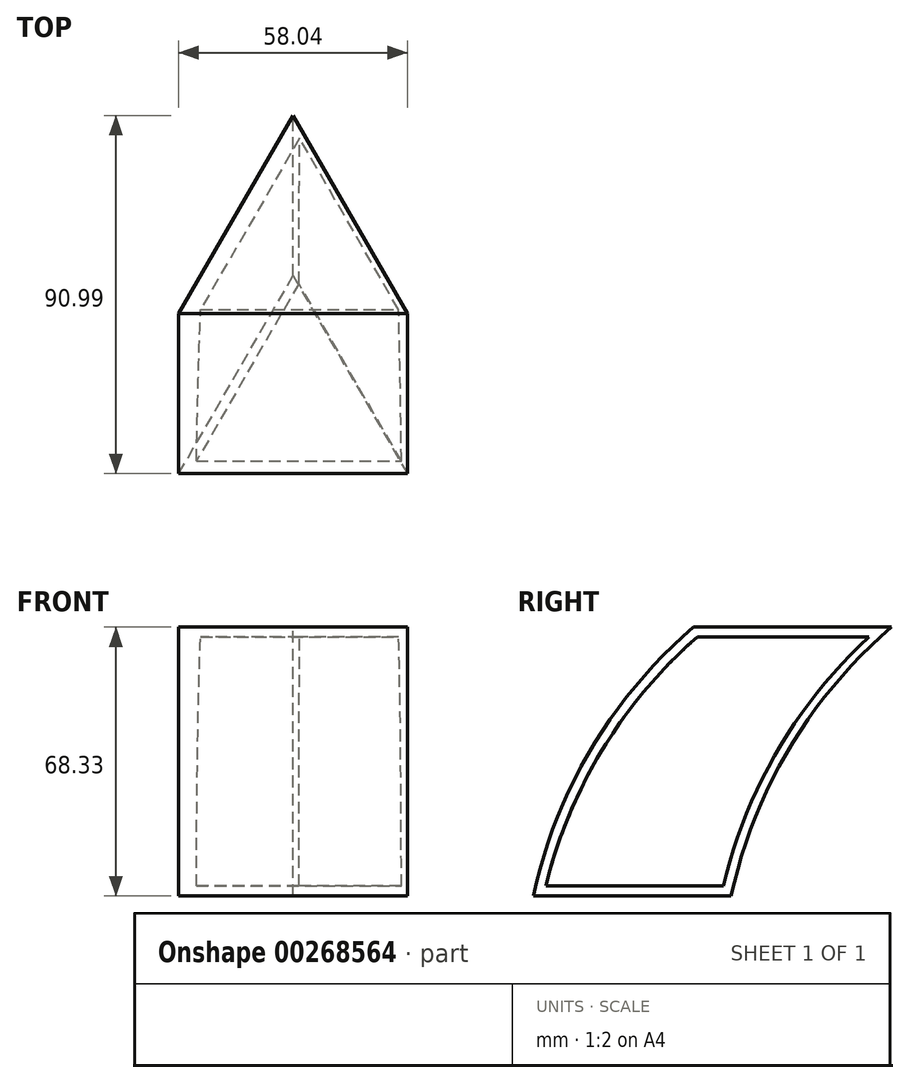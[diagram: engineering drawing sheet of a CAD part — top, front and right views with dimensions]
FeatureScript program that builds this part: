
annotation { "Feature Type Name" : "Feature", "Feature Type Description" : "" }
export const myFeature = defineFeature(function(context is Context, id is Id, definition is map)
    precondition{}
    {
        {
            var Q0;
            Q0=qCreatedBy(makeId("Top.planeOp"),FACE);
            var sketch = newSketch(context, id + "F0", { "sketchPlane" : qUnion([Q0])});
            skCircle(sketch, "E0.cCircle", {"center": v(0, 0) * mm, "radius": 16.76 * mm, "construction": true});
            skLineSegment(sketch, "E0.0", {"start": v(0, 33.51) * mm, "end": v(29.02, -16.76) * mm});
            skLineSegment(sketch, "E0.1", {"start": v(29.02, -16.76) * mm, "end": v(-29.02, -16.76) * mm});
            skLineSegment(sketch, "E0.2", {"start": v(-29.02, -16.76) * mm, "end": v(0, 33.51) * mm});
            skPoint(sketch, "E0.0.midPoint", {"position": v(14.51, 8.38) * mm});
            skSolve(sketch);
        }
        {
            var Q0;
            Q0=qCreatedBy(makeId("Right.planeOp"),FACE);
            var sketch = newSketch(context, id + "F1", { "sketchPlane" : qUnion([Q0])});
            skArc(sketch, "E1", {"start": v(74.23, 68.33) * mm, "mid": v(48.28, 37.5) * mm, "end": v(33.51, 0) * mm});
            skSolve(sketch);
        }
        {
            var Q0;
            Q0=makeQuery(id+"F0.imprint","IMPRINT",FACE,{"disambiguationData":[TD([[makeQuery(id+"F0.imprint","IMPRINT",EDGE,{"derivedFrom":sQuery(id+"F0.wireOp",EDGE,"E0.0")}),-1.0]])]});
            var Q1;
            Q1=sQuery(id+"F1.wireOp",EDGE,"E1");
            sweep(context, id + "F2", {"profiles" : qUnion([Q0]), "path" : qUnion([Q1]), "keepProfileOrientation" : true});
        }
        {
            var Q0;
            Q0=makeQuery(id+"F2.opSweep","SWEPT_FACE",FACE,{"disambiguationData":[OSD([sQuery(id+"F0.wireOp",EDGE,"E0.0"),sQuery(id+"F1.wireOp",EDGE,"E1")])]});
            shell(context, id + "F3", {"entities" : qUnion([Q0]), "thickness" : 2.54 * mm});
        }
    });
